# Revit family: P200921MX-011c_MED6230H_CW
name_source: partatom
category: Specialty Equipment
units: mm (PartAtom-declared; Revit-internal decimal feet)

## family parameters
Always vertical = No
Cut with Voids When Loaded = No
Enable Cutting in Views = No
Maintain Annotation Orientation = No
Part Type = Normal
Room Calculation Point = No
Round Connector Dimension = Use Diameter
Shared = No
Work Plane-Based = No

## types (2) — shared parameters
Accent Material = ARCAT - Plastic - Gray
Amps = 0 A
Back Panel Material = ARCAT - Metal - Aluminum
Clearance Material = ARCAT - Clearance
Default Elevation = 0"
Depth = 29 7/8"
Description = Smart Capable Top Load Electric Dryer with Extra Power Button - 7.4 cu. ft.
Dimension Guide = https://www.whirlpool.com
Display Material = ARCAT - Glass - Tempered - Dark - Black
Display Panel Material = ARCAT - Metal - Steel - Dark - Gray
Door Material = ARCAT - Glass - Tempered - Black
Family Name = Laundry
Feature 1 = Extra Power button
Feature 2 = Advanced Moisture Sensing
Feature 3 = Smart capable appliance
Glass Material = ARCAT - Glass - Tempered - Black
Handle Material = ARCAT - Metal - Steel - Stainless
Height = 41 1/4"
Knob Material = ARCAT - Metal - Steel - Stainless
Leg Material = ARCAT - Plastic - White
Manufacturer = Maytag
Voltage = 0 V
Width = 27"

## per-type parameters (varying)
| type | Body Material | Door Back Panel Material |
| MED6230HC | ARCAT - Metal - Steel - Gray | ARCAT - Metal - Steel - Black |
| MED6230HW | ARCAT - Metal - Steel - White | ARCAT - Metal - Steel - White |

note: column(s) folded — value = type name in every type: Model

## geometry (parser evidence)
native form markers: Sweep x7
no freeform markers — native parametric forms only
